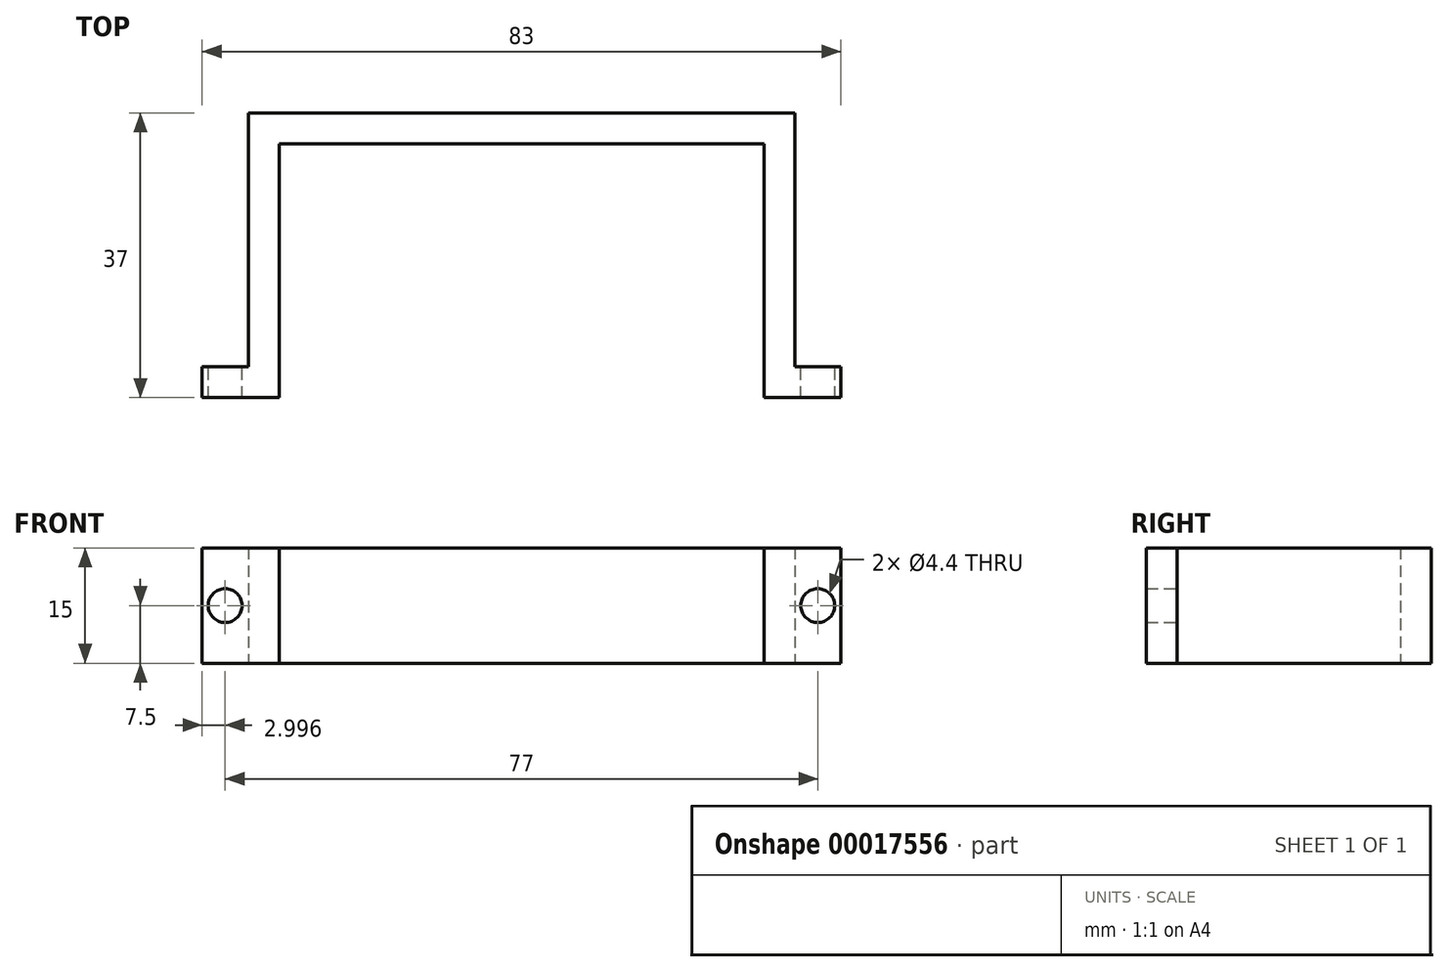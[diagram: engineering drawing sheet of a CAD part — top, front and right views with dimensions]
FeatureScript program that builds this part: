
annotation { "Feature Type Name" : "Feature", "Feature Type Description" : "" }
export const myFeature = defineFeature(function(context is Context, id is Id, definition is map)
    precondition{}
    {
        {
            var Q0;
            Q0=qCreatedBy(makeId("Top.planeOp"),FACE);
            var sketch = newSketch(context, id + "F0", { "sketchPlane" : qUnion([Q0])});
            skLineSegment(sketch, "E0", {"start": v(-13.02, 0) * mm, "end": v(-23.02, 0) * mm});
            skLineSegment(sketch, "E1", {"start": v(-23.02, 0) * mm, "end": v(-23.02, 4) * mm});
            skLineSegment(sketch, "E2", {"start": v(-23.02, 4) * mm, "end": v(-17.02, 4) * mm});
            skLineSegment(sketch, "E3", {"start": v(-17.02, 4) * mm, "end": v(-17.02, 37) * mm});
            skLineSegment(sketch, "E4", {"start": v(-17.02, 37) * mm, "end": v(53.98, 37) * mm});
            skLineSegment(sketch, "E5", {"start": v(53.98, 37) * mm, "end": v(53.98, 4) * mm});
            skLineSegment(sketch, "E6", {"start": v(53.98, 4) * mm, "end": v(59.98, 4) * mm});
            skLineSegment(sketch, "E7", {"start": v(59.98, 4) * mm, "end": v(59.98, 0) * mm});
            skLineSegment(sketch, "E8", {"start": v(59.98, 0) * mm, "end": v(49.98, 0) * mm});
            skLineSegment(sketch, "E9", {"start": v(49.98, 0) * mm, "end": v(49.98, 33) * mm});
            skLineSegment(sketch, "E10", {"start": v(49.98, 33) * mm, "end": v(-13.02, 33) * mm});
            skLineSegment(sketch, "E11", {"start": v(-13.02, 33) * mm, "end": v(-13.02, 0) * mm});
            skSolve(sketch);
        }
        {
            var Q0;
            Q0=qSketchRegion(id+"F0",true);
            extrude(context, id + "F1", {"entities" : qUnion([Q0]), "depth" : 15 * mm});
        }
        {
            var Q0;
            Q0=makeQuery(id+"F1.opExtrude","SWEPT_FACE",FACE,{"disambiguationData":[OSD([sQuery(id+"F0.wireOp",EDGE,"E2")])]});
            var sketch = newSketch(context, id + "F2", { "sketchPlane" : qUnion([Q0])});
            skLineSegment(sketch, "E12", {"start": v(23.02, 7.5) * mm, "end": v(17.02, 7.5) * mm});
            skCircle(sketch, "E13", {"center": v(20.02, 7.5) * mm, "radius": 2.2 * mm});
            skSolve(sketch);
        }
        {
            var Q0;
            Q0=qSketchRegion(id+"F2",true);
            extrude(context, id + "F3", {"entities" : qUnion([Q0]), "operationType" : NewBodyOperationType.REMOVE, "oppositeDirection" : true, "depth" : 25 * mm});
        }
        {
            var Q0;
            Q0=makeQuery(id+"F1.opExtrude","SWEPT_FACE",FACE,{"disambiguationData":[OSD([sQuery(id+"F0.wireOp",EDGE,"E6")])]});
            var sketch = newSketch(context, id + "F4", { "sketchPlane" : qUnion([Q0])});
            skLineSegment(sketch, "E14", {"start": v(-53.98, 7.5) * mm, "end": v(-59.98, 7.5) * mm});
            skCircle(sketch, "E15", {"center": v(-56.98, 7.5) * mm, "radius": 2.2 * mm});
            skSolve(sketch);
        }
        {
            var Q0;
            Q0=qSketchRegion(id+"F4",true);
            extrude(context, id + "F5", {"entities" : qUnion([Q0]), "operationType" : NewBodyOperationType.REMOVE, "oppositeDirection" : true, "depth" : 25 * mm});
        }
    });
